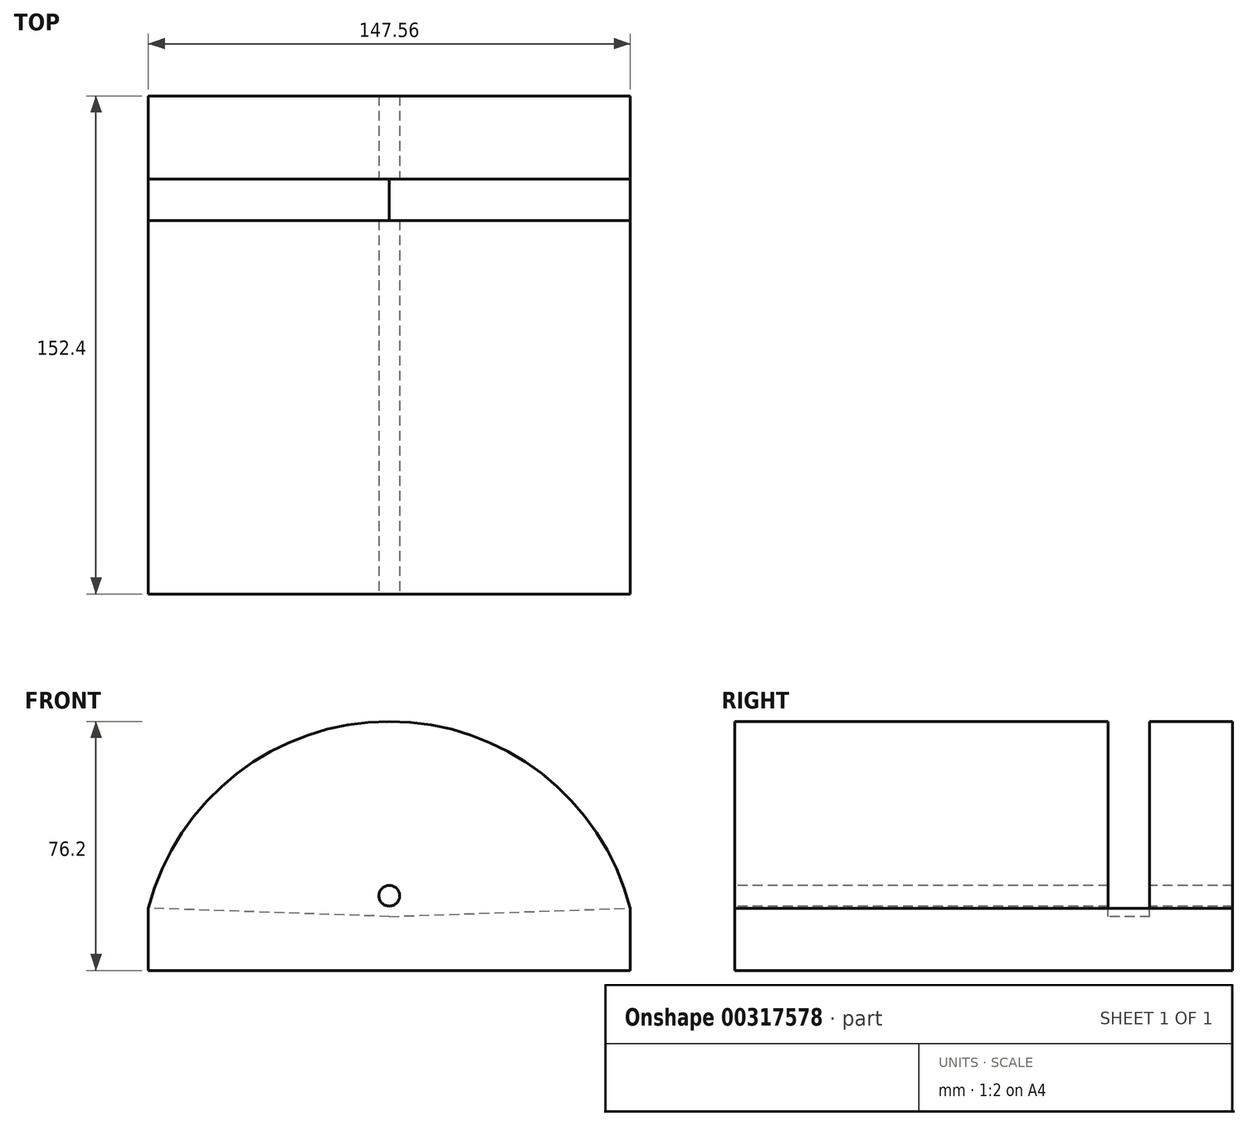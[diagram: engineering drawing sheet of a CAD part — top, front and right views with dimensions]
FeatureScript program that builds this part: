
annotation { "Feature Type Name" : "Feature", "Feature Type Description" : "" }
export const myFeature = defineFeature(function(context is Context, id is Id, definition is map)
    precondition{}
    {
        {
            var Q0;
            Q0=qCreatedBy(makeId("Front.planeOp"),FACE);
            var sketch = newSketch(context, id + "F0", { "sketchPlane" : qUnion([Q0])});
            skArc(sketch, "E0", {"start": v(73.78, 19.05) * mm, "mid": v(0, 76.2) * mm, "end": v(-73.78, 19.05) * mm});
            skLineSegment(sketch, "E1.top", {"start": v(-73.78, 0) * mm, "end": v(73.78, 0) * mm});
            skLineSegment(sketch, "E1.left", {"start": v(-73.78, 19.05) * mm, "end": v(-73.78, 0) * mm});
            skLineSegment(sketch, "E1.right", {"start": v(73.78, 19.05) * mm, "end": v(73.78, 0) * mm});
            skPoint(sketch, "E2", {"position": v(0, 16.51) * mm});
            skLineSegment(sketch, "E3", {"start": v(0, 16.51) * mm, "end": v(73.78, 19.05) * mm});
            skLineSegment(sketch, "E4", {"start": v(0, 16.51) * mm, "end": v(-73.78, 19.05) * mm});
            skSolve(sketch);
        }
        {
            var Q0;
            {var subQ0=sQuery(id+"F0.wireOp",EDGE,"E1.left");Q0=makeQuery(id+"F0.imprint","IMPRINT",FACE,{"disambiguationData":[TD([[makeQuery(id+"F0.imprint","IMPRINT",EDGE,{"derivedFrom":subQ0}),1.0]])]});}
            var Q1;
            {var subQ0=sQuery(id+"F0.wireOp",EDGE,"E1.right");Q1=makeQuery(id+"F0.imprint","IMPRINT",FACE,{"disambiguationData":[TD([[makeQuery(id+"F0.imprint","IMPRINT",EDGE,{"derivedFrom":subQ0}),-1.0]])]});}
            var Q2;
            Q2=makeQuery(id+"F0.imprint","IMPRINT",FACE,{"disambiguationData":[TD([[makeQuery(id+"F0.imprint","IMPRINT",EDGE,{"derivedFrom":sQuery(id+"F0.wireOp",EDGE,"E0")}),1.0]])]});
            extrude(context, id + "F1", {"entities" : qUnion([Q0, Q1, Q2]), "endBound" : BoundingType.SYMMETRIC, "depth" : 152.4 * mm, "offsetDistance" : 25.4 * mm});
        }
        {
            var Q0;
            Q0=makeQuery(id+"F0.imprint","IMPRINT",FACE,{"disambiguationData":[TD([[makeQuery(id+"F0.imprint","IMPRINT",EDGE,{"derivedFrom":sQuery(id+"F0.wireOp",EDGE,"E0")}),1.0]])]});
            extrude(context, id + "F2", {"entities" : qUnion([Q0]), "operationType" : NewBodyOperationType.REMOVE, "oppositeDirection" : true, "depth" : 50.8 * mm, "offsetDistance" : 25.4 * mm, "hasSecondDirection" : true, "secondDirectionOppositeDirection" : true, "secondDirectionDepth" : 38.1 * mm});
        }
        {
            var Q0;
            Q0=makeQuery(id+"F1.opExtrude","CAP_FACE",FACE,{"disambiguationData":[OSD([sQuery(id+"F0.wireOp",EDGE,"E0"),sQuery(id+"F0.wireOp",EDGE,"E1.top"),sQuery(id+"F0.wireOp",EDGE,"E1.left"),sQuery(id+"F0.wireOp",EDGE,"E1.right")])],"isStart":false});
            var sketch = newSketch(context, id + "F3", { "sketchPlane" : qUnion([Q0])});
            skCircle(sketch, "E5", {"center": v(0, 22.86) * mm, "radius": 3.18 * mm});
            skSolve(sketch);
        }
        {
            var Q0;
            Q0=makeQuery(id+"F3.imprint","IMPRINT",FACE,{"disambiguationData":[TD([[makeQuery(id+"F3.imprint","IMPRINT",EDGE,{"derivedFrom":sQuery(id+"F3.wireOp",EDGE,"E5")}),1.0]])]});
            extrude(context, id + "F4", {"entities" : qUnion([Q0]), "operationType" : NewBodyOperationType.REMOVE, "oppositeDirection" : true, "depth" : 152.4 * mm, "offsetDistance" : 25.4 * mm});
        }
    });
